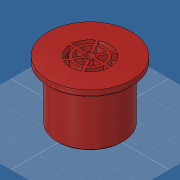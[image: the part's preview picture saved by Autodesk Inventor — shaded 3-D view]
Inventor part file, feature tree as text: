
AUTODESK INVENTOR PART (.ipt)
format: ipt  version: 2019 (Build 230136000, 136)  size: 281,600 bytes
history: native  units: mm
features: sketch x3, extrude x2, revolve x1, chamfer x1, projected_geometry x1
ambient origin geometry x8: Origin, YZ Plane, XZ Plane, XY Plane, X Axis, Y Axis, Z Axis, Center Point
bodies: Volumenkörper1 (feature_tree)
feature tree (8):
  revolve  "Umdrehung1"
  sketch  "Skizze2"  dims[d4=5.0mm]
  extrude  "Extrusion1"  Depth=3.0mm
  chamfer  "Fase1"  Distance=50.0mm
  extrude  "Extrusion5"  Depth=10.0mm
  sketch  "Skizze1"  dims[d2=60.0deg d3=3.0mm]
  sketch  "Skizze3"  dims[d5=7.0mm d6=50.0mm d7=40.0mm d8=63.5mm d11=90.0deg d19=5.0mm d20=0.0mm d25=19.0mm d26=23.0mm d28=8.0mm d29=6.0mm d30=2.0mm d38=5.0mm d39=60.0mm d41=360.0deg d43=1.0mm d44=2.0mm d45=45.0deg d47=30.0mm d51=18.0mm d52=10.0mm d53=0.0mm d54=60.0mm d56=360.0deg]
  projected_geometry  "Projizierte Kontur1"
